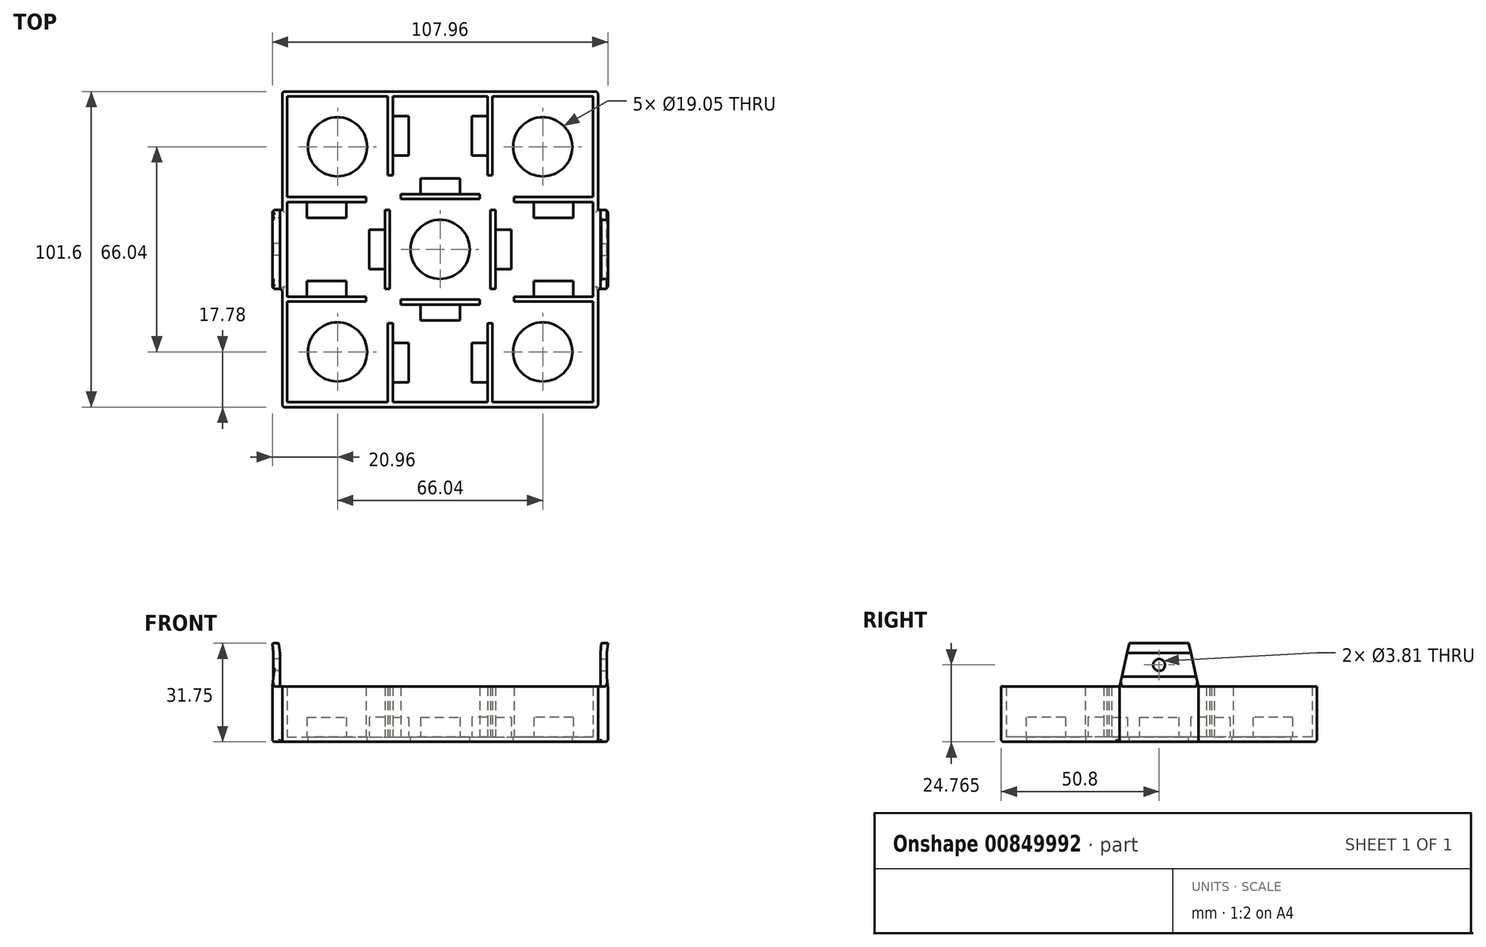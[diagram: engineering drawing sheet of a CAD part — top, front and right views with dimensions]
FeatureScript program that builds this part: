
annotation { "Feature Type Name" : "Feature", "Feature Type Description" : "" }
export const myFeature = defineFeature(function(context is Context, id is Id, definition is map)
    precondition{}
    {
        {
            var Q0;
            Q0=qCreatedBy(makeId("Top.planeOp"),FACE);
            var sketch = newSketch(context, id + "F0", { "sketchPlane" : qUnion([Q0])});
            skLineSegment(sketch, "E0.bottom", {"start": v(-50.8, 50.8) * mm, "end": v(50.8, 50.8) * mm});
            skLineSegment(sketch, "E0.top", {"start": v(-50.8, -50.8) * mm, "end": v(50.8, -50.8) * mm});
            skLineSegment(sketch, "E0.left", {"start": v(-50.8, 50.8) * mm, "end": v(-50.8, -50.8) * mm});
            skLineSegment(sketch, "E0.right", {"start": v(50.8, 50.8) * mm, "end": v(50.8, -50.8) * mm});
            skLineSegment(sketch, "E1", {"start": v(-50.8, 50.8) * mm, "end": v(50.8, -50.8) * mm, "construction": true});
            skSolve(sketch);
        }
        {
            var Q0;
            Q0=qSketchRegion(id+"F0",true);
            extrude(context, id + "F1", {"entities" : qUnion([Q0]), "depth" : 1.59 * mm, "offsetDistance" : 25.4 * mm});
        }
        {
            var Q0;
            Q0=makeQuery(id+"F1.opExtrude","CAP_FACE",FACE,{"disambiguationData":[OSD([sQuery(id+"F0.wireOp",EDGE,"E0.bottom"),sQuery(id+"F0.wireOp",EDGE,"E0.top"),sQuery(id+"F0.wireOp",EDGE,"E0.left"),sQuery(id+"F0.wireOp",EDGE,"E0.right")])],"isStart":false});
            var sketch = newSketch(context, id + "F2", { "sketchPlane" : qUnion([Q0])});
            skLineSegment(sketch, "E2.bottom", {"start": v(-50.8, 50.8) * mm, "end": v(50.8, 50.8) * mm});
            skLineSegment(sketch, "E2.top", {"start": v(-50.8, -50.8) * mm, "end": v(50.8, -50.8) * mm});
            skLineSegment(sketch, "E2.left", {"start": v(-50.8, 50.8) * mm, "end": v(-50.8, -50.8) * mm});
            skLineSegment(sketch, "E2.right", {"start": v(50.8, 50.8) * mm, "end": v(50.8, -50.8) * mm});
            skLineSegment(sketch, "E3.0", {"start": v(49.21, 49.21) * mm, "end": v(49.21, -49.21) * mm});
            skLineSegment(sketch, "E3.1", {"start": v(-49.21, 49.21) * mm, "end": v(49.21, 49.21) * mm});
            skLineSegment(sketch, "E3.2", {"start": v(-49.21, 49.21) * mm, "end": v(-49.21, -49.21) * mm});
            skLineSegment(sketch, "E3.3", {"start": v(-49.21, -49.21) * mm, "end": v(49.21, -49.21) * mm});
            skSolve(sketch);
        }
        {
            var Q0;
            Q0=qSketchRegion(id+"F2",true);
            extrude(context, id + "F3", {"entities" : qUnion([Q0]), "operationType" : NewBodyOperationType.ADD, "depth" : 16.2 * mm, "offsetDistance" : 25.4 * mm});
        }
        {
            var Q0;
            Q0=makeQuery(id+"F1.opExtrude","CAP_FACE",FACE,{"disambiguationData":[OSD([sQuery(id+"F0.wireOp",EDGE,"E0.bottom"),sQuery(id+"F0.wireOp",EDGE,"E0.top"),sQuery(id+"F0.wireOp",EDGE,"E0.left"),sQuery(id+"F0.wireOp",EDGE,"E0.right")])],"isStart":false});
            var sketch = newSketch(context, id + "F4", { "sketchPlane" : qUnion([Q0])});
            skLineSegment(sketch, "E4", {"start": v(-49.21, -16.83) * mm, "end": v(-23.81, -16.83) * mm});
            skLineSegment(sketch, "E5", {"start": v(-49.21, -15.24) * mm, "end": v(-23.81, -15.24) * mm});
            skLineSegment(sketch, "E6", {"start": v(-49.21, -15.24) * mm, "end": v(-49.21, -16.83) * mm});
            skLineSegment(sketch, "E7", {"start": v(49.21, -15.24) * mm, "end": v(49.21, -16.83) * mm});
            skLineSegment(sketch, "E8.bottom", {"start": v(-49.21, 16.83) * mm, "end": v(-23.81, 16.83) * mm});
            skLineSegment(sketch, "E8.top", {"start": v(-49.21, 15.24) * mm, "end": v(-23.81, 15.24) * mm});
            skLineSegment(sketch, "E8.left", {"start": v(-49.21, 16.83) * mm, "end": v(-49.21, 15.24) * mm});
            skLineSegment(sketch, "E8.right", {"start": v(49.21, 16.83) * mm, "end": v(49.21, 15.24) * mm});
            skLineSegment(sketch, "E9.bottom", {"start": v(15.24, 49.21) * mm, "end": v(16.83, 49.21) * mm});
            skLineSegment(sketch, "E9.left", {"start": v(15.24, 49.21) * mm, "end": v(15.24, 23.81) * mm});
            skLineSegment(sketch, "E9.right", {"start": v(16.83, 49.21) * mm, "end": v(16.83, 23.81) * mm});
            skLineSegment(sketch, "E10.bottom", {"start": v(-16.83, 49.21) * mm, "end": v(-15.24, 49.21) * mm});
            skLineSegment(sketch, "E10.left", {"start": v(-16.83, 49.21) * mm, "end": v(-16.83, 23.81) * mm});
            skLineSegment(sketch, "E10.right", {"start": v(-15.24, 49.21) * mm, "end": v(-15.24, 23.81) * mm});
            skLineSegment(sketch, "E11.top", {"start": v(-16.83, -49.21) * mm, "end": v(-15.24, -49.21) * mm});
            skLineSegment(sketch, "E11.left", {"start": v(-16.83, -23.81) * mm, "end": v(-16.83, -49.21) * mm});
            skLineSegment(sketch, "E11.right", {"start": v(-15.24, -23.81) * mm, "end": v(-15.24, -49.21) * mm});
            skLineSegment(sketch, "E12.top", {"start": v(15.24, -49.21) * mm, "end": v(16.83, -49.21) * mm});
            skLineSegment(sketch, "E12.left", {"start": v(15.24, -23.81) * mm, "end": v(15.24, -49.21) * mm});
            skLineSegment(sketch, "E12.right", {"start": v(16.83, -23.81) * mm, "end": v(16.83, -49.21) * mm});
            skLineSegment(sketch, "E13", {"start": v(-23.81, 16.83) * mm, "end": v(-23.81, 15.24) * mm});
            skLineSegment(sketch, "E14", {"start": v(-16.83, 23.81) * mm, "end": v(-15.24, 23.81) * mm});
            skLineSegment(sketch, "E15", {"start": v(15.24, 23.81) * mm, "end": v(16.83, 23.81) * mm});
            skLineSegment(sketch, "E16", {"start": v(23.81, 16.83) * mm, "end": v(23.81, 15.24) * mm});
            skLineSegment(sketch, "E17.trimOffspring", {"start": v(23.81, 16.83) * mm, "end": v(49.21, 16.83) * mm});
            skLineSegment(sketch, "E18.trimOffspring", {"start": v(23.81, 15.24) * mm, "end": v(49.21, 15.24) * mm});
            skLineSegment(sketch, "E19", {"start": v(-16.83, -23.81) * mm, "end": v(-15.24, -23.81) * mm});
            skLineSegment(sketch, "E20", {"start": v(-23.81, -15.24) * mm, "end": v(-23.81, -16.83) * mm});
            skLineSegment(sketch, "E21", {"start": v(49.21, -15.24) * mm, "end": v(23.81, -15.24) * mm});
            skLineSegment(sketch, "E22", {"start": v(23.81, -15.24) * mm, "end": v(23.81, -16.83) * mm});
            skLineSegment(sketch, "E23", {"start": v(23.81, -16.83) * mm, "end": v(49.21, -16.83) * mm});
            skLineSegment(sketch, "E24", {"start": v(15.24, -23.81) * mm, "end": v(16.83, -23.81) * mm});
            skLineSegment(sketch, "E25.bottom", {"start": v(-12.7, 16.2) * mm, "end": v(12.7, 16.2) * mm});
            skLineSegment(sketch, "E25.top", {"start": v(-12.7, -16.2) * mm, "end": v(12.7, -16.2) * mm});
            skLineSegment(sketch, "E25.left", {"start": v(-16.2, 12.7) * mm, "end": v(-16.2, -12.7) * mm});
            skLineSegment(sketch, "E25.right", {"start": v(16.2, 12.7) * mm, "end": v(16.2, -12.7) * mm});
            skLineSegment(sketch, "E26", {"start": v(-12.7, 16.2) * mm, "end": v(-12.7, 17.78) * mm});
            skLineSegment(sketch, "E27", {"start": v(-12.7, 17.78) * mm, "end": v(12.7, 17.78) * mm});
            skLineSegment(sketch, "E28", {"start": v(12.7, 17.78) * mm, "end": v(12.7, 16.2) * mm});
            skLineSegment(sketch, "E29", {"start": v(0, 17.78) * mm, "end": v(0, 16.2) * mm, "construction": true});
            skLineSegment(sketch, "E30", {"start": v(-12.7, -16.2) * mm, "end": v(-12.7, -17.78) * mm});
            skLineSegment(sketch, "E31", {"start": v(-12.7, -17.78) * mm, "end": v(12.7, -17.78) * mm});
            skLineSegment(sketch, "E32", {"start": v(12.7, -17.78) * mm, "end": v(12.7, -16.2) * mm});
            skLineSegment(sketch, "E33", {"start": v(0, -16.2) * mm, "end": v(0, -17.78) * mm, "construction": true});
            skLineSegment(sketch, "E34", {"start": v(16.2, 12.7) * mm, "end": v(17.78, 12.7) * mm});
            skLineSegment(sketch, "E35", {"start": v(17.78, 12.7) * mm, "end": v(17.78, -12.7) * mm});
            skLineSegment(sketch, "E36", {"start": v(17.78, -12.7) * mm, "end": v(16.2, -12.7) * mm});
            skLineSegment(sketch, "E37", {"start": v(16.2, 0) * mm, "end": v(17.78, 0) * mm, "construction": true});
            skLineSegment(sketch, "E38", {"start": v(-16.2, -12.7) * mm, "end": v(-17.78, -12.7) * mm});
            skLineSegment(sketch, "E39", {"start": v(-17.78, -12.7) * mm, "end": v(-17.78, 12.7) * mm});
            skLineSegment(sketch, "E40", {"start": v(-17.78, 12.7) * mm, "end": v(-16.2, 12.7) * mm});
            skLineSegment(sketch, "E41", {"start": v(-16.2, 0) * mm, "end": v(-17.78, 0) * mm, "construction": true});
            skLineSegment(sketch, "E42", {"start": v(0, 16.2) * mm, "end": v(0, 0) * mm, "construction": true});
            skLineSegment(sketch, "E43", {"start": v(0, 0) * mm, "end": v(0, -16.2) * mm, "construction": true});
            skLineSegment(sketch, "E44", {"start": v(-16.2, 0) * mm, "end": v(0, 0) * mm, "construction": true});
            skLineSegment(sketch, "E45", {"start": v(16.2, 0) * mm, "end": v(0, 0) * mm, "construction": true});
            skLineSegment(sketch, "E46", {"start": v(0, 49.21) * mm, "end": v(0, 17.78) * mm, "construction": true});
            skLineSegment(sketch, "E47", {"start": v(0, -17.78) * mm, "end": v(0, -49.21) * mm, "construction": true});
            skLineSegment(sketch, "E48", {"start": v(-49.21, 0) * mm, "end": v(-17.78, 0) * mm, "construction": true});
            skLineSegment(sketch, "E49", {"start": v(17.78, 0) * mm, "end": v(49.21, 0) * mm, "construction": true});
            skSolve(sketch);
        }
        {
            var Q0;
            Q0=qSketchRegion(id+"F4",true);
            var Q1;
            Q1=makeQuery(id+"F3.opExtrude","CAP_FACE",FACE,{"disambiguationData":[OSD([sQuery(id+"F2.wireOp",EDGE,"E2.bottom"),sQuery(id+"F2.wireOp",EDGE,"E2.top"),sQuery(id+"F2.wireOp",EDGE,"E2.left"),sQuery(id+"F2.wireOp",EDGE,"E2.right"),sQuery(id+"F2.wireOp",EDGE,"E3.0"),sQuery(id+"F2.wireOp",EDGE,"E3.1"),sQuery(id+"F2.wireOp",EDGE,"E3.2"),sQuery(id+"F2.wireOp",EDGE,"E3.3")])],"isStart":false});
            extrude(context, id + "F5", {"entities" : qUnion([Q0]), "operationType" : NewBodyOperationType.ADD, "endBound" : BoundingType.UP_TO_SURFACE, "depth" : 25.4 * mm, "endBoundEntityFace" : qUnion([Q1]), "offsetDistance" : 25.4 * mm});
        }
        {
            var Q0;
            Q0=makeQuery(id+"F1.opExtrude","CAP_FACE",FACE,{"disambiguationData":[OSD([sQuery(id+"F0.wireOp",EDGE,"E0.bottom"),sQuery(id+"F0.wireOp",EDGE,"E0.top"),sQuery(id+"F0.wireOp",EDGE,"E0.left"),sQuery(id+"F0.wireOp",EDGE,"E0.right")])],"isStart":false});
            var sketch = newSketch(context, id + "F6", { "sketchPlane" : qUnion([Q0])});
            skLineSegment(sketch, "E50.bottom", {"start": v(-42.86, 15.24) * mm, "end": v(-30.16, 15.24) * mm});
            skLineSegment(sketch, "E50.top", {"start": v(-42.86, 10.16) * mm, "end": v(-30.16, 10.16) * mm});
            skLineSegment(sketch, "E50.left", {"start": v(-42.86, 15.24) * mm, "end": v(-42.86, 10.16) * mm});
            skLineSegment(sketch, "E50.right", {"start": v(-30.16, 15.24) * mm, "end": v(-30.16, 10.16) * mm});
            skLineSegment(sketch, "E51.bottom", {"start": v(-42.86, -15.24) * mm, "end": v(-30.16, -15.24) * mm});
            skLineSegment(sketch, "E51.top", {"start": v(-42.86, -10.16) * mm, "end": v(-30.16, -10.16) * mm});
            skLineSegment(sketch, "E51.left", {"start": v(-42.86, -15.24) * mm, "end": v(-42.86, -10.16) * mm});
            skLineSegment(sketch, "E51.right", {"start": v(-30.16, -15.24) * mm, "end": v(-30.16, -10.16) * mm});
            skLineSegment(sketch, "E52.bottom", {"start": v(-15.24, 42.86) * mm, "end": v(-10.16, 42.86) * mm});
            skLineSegment(sketch, "E52.top", {"start": v(-15.24, 30.16) * mm, "end": v(-10.16, 30.16) * mm});
            skLineSegment(sketch, "E52.left", {"start": v(-15.24, 42.86) * mm, "end": v(-15.24, 30.16) * mm});
            skLineSegment(sketch, "E52.right", {"start": v(-10.16, 42.86) * mm, "end": v(-10.16, 30.16) * mm});
            skLineSegment(sketch, "E53.bottom", {"start": v(15.24, 42.86) * mm, "end": v(10.16, 42.86) * mm});
            skLineSegment(sketch, "E53.top", {"start": v(15.24, 30.16) * mm, "end": v(10.16, 30.16) * mm});
            skLineSegment(sketch, "E53.left", {"start": v(15.24, 42.86) * mm, "end": v(15.24, 30.16) * mm});
            skLineSegment(sketch, "E53.right", {"start": v(10.16, 42.86) * mm, "end": v(10.16, 30.16) * mm});
            skLineSegment(sketch, "E54.bottom", {"start": v(30.16, 15.24) * mm, "end": v(42.86, 15.24) * mm});
            skLineSegment(sketch, "E54.top", {"start": v(30.16, 10.16) * mm, "end": v(42.86, 10.16) * mm});
            skLineSegment(sketch, "E54.left", {"start": v(30.16, 15.24) * mm, "end": v(30.16, 10.16) * mm});
            skLineSegment(sketch, "E54.right", {"start": v(42.86, 15.24) * mm, "end": v(42.86, 10.16) * mm});
            skLineSegment(sketch, "E55.bottom", {"start": v(30.16, -15.24) * mm, "end": v(42.86, -15.24) * mm});
            skLineSegment(sketch, "E55.top", {"start": v(30.16, -10.16) * mm, "end": v(42.86, -10.16) * mm});
            skLineSegment(sketch, "E55.left", {"start": v(30.16, -15.24) * mm, "end": v(30.16, -10.16) * mm});
            skLineSegment(sketch, "E55.right", {"start": v(42.86, -15.24) * mm, "end": v(42.86, -10.16) * mm});
            skLineSegment(sketch, "E56.bottom", {"start": v(15.24, -30.16) * mm, "end": v(10.16, -30.16) * mm});
            skLineSegment(sketch, "E56.top", {"start": v(15.24, -42.86) * mm, "end": v(10.16, -42.86) * mm});
            skLineSegment(sketch, "E56.left", {"start": v(15.24, -30.16) * mm, "end": v(15.24, -42.86) * mm});
            skLineSegment(sketch, "E56.right", {"start": v(10.16, -30.16) * mm, "end": v(10.16, -42.86) * mm});
            skLineSegment(sketch, "E57.bottom", {"start": v(-15.24, -30.16) * mm, "end": v(-10.16, -30.16) * mm});
            skLineSegment(sketch, "E57.top", {"start": v(-15.24, -42.86) * mm, "end": v(-10.16, -42.86) * mm});
            skLineSegment(sketch, "E57.left", {"start": v(-15.24, -30.16) * mm, "end": v(-15.24, -42.86) * mm});
            skLineSegment(sketch, "E57.right", {"start": v(-10.16, -30.16) * mm, "end": v(-10.16, -42.86) * mm});
            skLineSegment(sketch, "E58.bottom", {"start": v(-6.35, -17.78) * mm, "end": v(6.35, -17.78) * mm});
            skLineSegment(sketch, "E58.top", {"start": v(-6.35, -22.86) * mm, "end": v(6.35, -22.86) * mm});
            skLineSegment(sketch, "E58.left", {"start": v(-6.35, -17.78) * mm, "end": v(-6.35, -22.86) * mm});
            skLineSegment(sketch, "E58.right", {"start": v(6.35, -17.78) * mm, "end": v(6.35, -22.86) * mm});
            skLineSegment(sketch, "E59.bottom", {"start": v(17.78, 6.35) * mm, "end": v(22.86, 6.35) * mm});
            skLineSegment(sketch, "E59.top", {"start": v(17.78, -6.35) * mm, "end": v(22.86, -6.35) * mm});
            skLineSegment(sketch, "E59.left", {"start": v(17.78, 6.35) * mm, "end": v(17.78, -6.35) * mm});
            skLineSegment(sketch, "E59.right", {"start": v(22.86, 6.35) * mm, "end": v(22.86, -6.35) * mm});
            skLineSegment(sketch, "E60.bottom", {"start": v(-17.78, 6.35) * mm, "end": v(-22.86, 6.35) * mm});
            skLineSegment(sketch, "E60.left", {"start": v(-17.78, 6.35) * mm, "end": v(-17.78, -6.35) * mm});
            skLineSegment(sketch, "E61.bottom", {"start": v(-6.35, 17.78) * mm, "end": v(6.35, 17.78) * mm});
            skLineSegment(sketch, "E61.top", {"start": v(-6.35, 22.86) * mm, "end": v(6.35, 22.86) * mm});
            skLineSegment(sketch, "E61.left", {"start": v(-6.35, 17.78) * mm, "end": v(-6.35, 22.86) * mm});
            skLineSegment(sketch, "E61.right", {"start": v(6.35, 17.78) * mm, "end": v(6.35, 22.86) * mm});
            skLineSegment(sketch, "E62", {"start": v(-22.86, 6.35) * mm, "end": v(-22.86, -6.35) * mm});
            skLineSegment(sketch, "E63", {"start": v(-22.86, -6.35) * mm, "end": v(-17.78, -6.35) * mm});
            skSolve(sketch);
        }
        {
            var Q0;
            Q0=qSketchRegion(id+"F6",true);
            extrude(context, id + "F7", {"entities" : qUnion([Q0]), "operationType" : NewBodyOperationType.ADD, "depth" : 6.35 * mm, "offsetDistance" : 25.4 * mm});
        }
        {
            var Q0;
            Q0=makeQuery(id+"F1.opExtrude","CAP_FACE",FACE,{"disambiguationData":[OSD([sQuery(id+"F0.wireOp",EDGE,"E0.bottom"),sQuery(id+"F0.wireOp",EDGE,"E0.top"),sQuery(id+"F0.wireOp",EDGE,"E0.left"),sQuery(id+"F0.wireOp",EDGE,"E0.right")])],"isStart":false});
            var sketch = newSketch(context, id + "F8", { "sketchPlane" : qUnion([Q0])});
            skCircle(sketch, "E64", {"center": v(0, 0) * mm, "radius": 9.53 * mm});
            skCircle(sketch, "E65", {"center": v(-33.02, 33.02) * mm, "radius": 9.53 * mm});
            skCircle(sketch, "E66", {"center": v(33.02, 33.02) * mm, "radius": 9.53 * mm});
            skCircle(sketch, "E67", {"center": v(33.02, -33.02) * mm, "radius": 9.53 * mm});
            skCircle(sketch, "E68", {"center": v(-33.02, -33.02) * mm, "radius": 9.53 * mm});
            skPoint(sketch, "E68.centerSnap0", {"position": v(-16.83, -36.51) * mm});
            skSolve(sketch);
        }
        {
            var Q0;
            Q0 = qSketchRegion(id + "F8", true);
            extrude(context, id + "F9", {"entities" : qUnion([Q0]), "operationType" : NewBodyOperationType.REMOVE, "oppositeDirection" : true, "depth" : 25.4 * mm, "offsetDistance" : 25.4 * mm});
        }
        {
            var Q0;
            Q0=qCreatedBy(makeId("Front.planeOp"),FACE);
            var sketch = newSketch(context, id + "F10", { "sketchPlane" : qUnion([Q0])});
            skLineSegment(sketch, "E69.bottom", {"start": v(53.98, 0) * mm, "end": v(50.8, 0) * mm});
            skLineSegment(sketch, "E69.top", {"start": v(53.98, 31.75) * mm, "end": v(51.91, 31.75) * mm});
            skLineSegment(sketch, "E69.left", {"start": v(53.98, 0) * mm, "end": v(53.98, 17.78) * mm});
            skLineSegment(sketch, "E69.right", {"start": v(50.8, 0) * mm, "end": v(50.8, 17.78) * mm});
            skLineSegment(sketch, "E70", {"start": v(51.91, 31.75) * mm, "end": v(51.56, 28.57) * mm});
            skLineSegment(sketch, "E71", {"start": v(51.56, 28.58) * mm, "end": v(51.56, 17.78) * mm});
            skLineSegment(sketch, "E72", {"start": v(51.56, 17.78) * mm, "end": v(50.8, 17.78) * mm});
            skLineSegment(sketch, "E73", {"start": v(53.98, 31.75) * mm, "end": v(53.63, 28.57) * mm});
            skLineSegment(sketch, "E74", {"start": v(53.63, 28.57) * mm, "end": v(53.63, 20.96) * mm});
            skLineSegment(sketch, "E75", {"start": v(53.63, 20.96) * mm, "end": v(53.98, 17.78) * mm});
            skSolve(sketch);
        }
        {
            var Q0;
            Q0 = qSketchRegion(id + "F10", true);
            extrude(context, id + "F11", {"entities" : qUnion([Q0]), "operationType" : NewBodyOperationType.ADD, "endBound" : BoundingType.SYMMETRIC, "depth" : 25.4 * mm, "offsetDistance" : 25.4 * mm});
        }
        {
            var Q0;
            Q0=makeQuery(id+"F11.opExtrude","SWEPT_FACE",FACE,{"disambiguationData":[OSD([sQuery(id+"F10.wireOp",EDGE,"E69.left")])]});
            var sketch = newSketch(context, id + "F12", { "sketchPlane" : qUnion([Q0])});
            skLineSegment(sketch, "E76", {"start": v(-12.7, 17.78) * mm, "end": v(-9.53, 31.75) * mm});
            skLineSegment(sketch, "E77", {"start": v(-9.53, 31.75) * mm, "end": v(-12.7, 31.75) * mm});
            skLineSegment(sketch, "E78", {"start": v(-12.7, 31.75) * mm, "end": v(-12.7, 17.78) * mm});
            skLineSegment(sketch, "E79", {"start": v(12.7, 17.78) * mm, "end": v(9.52, 31.75) * mm});
            skLineSegment(sketch, "E80", {"start": v(9.53, 31.75) * mm, "end": v(12.7, 31.75) * mm});
            skLineSegment(sketch, "E81", {"start": v(12.7, 31.75) * mm, "end": v(12.7, 17.78) * mm});
            skSolve(sketch);
        }
        {
            var Q0;
            Q0 = qSketchRegion(id + "F12", true);
            extrude(context, id + "F13", {"entities" : qUnion([Q0]), "operationType" : NewBodyOperationType.REMOVE, "oppositeDirection" : true, "depth" : 3.17 * mm, "offsetDistance" : 25.4 * mm});
        }
        {
            var Q0;
            Q0=makeQuery(id+"F11.opExtrude","SWEPT_FACE",FACE,{"disambiguationData":[OSD([sQuery(id+"F10.wireOp",EDGE,"E74")])]});
            var sketch = newSketch(context, id + "F14", { "sketchPlane" : qUnion([Q0])});
            skCircle(sketch, "E82", {"center": v(0, 24.76) * mm, "radius": 1.9 * mm});
            skLineSegment(sketch, "E83", {"start": v(0, 28.57) * mm, "end": v(0, 24.76) * mm, "construction": true});
            skLineSegment(sketch, "E84", {"start": v(0, 20.95) * mm, "end": v(0, 24.76) * mm, "construction": true});
            skSolve(sketch);
        }
        {
            var Q0;
            Q0 = qSketchRegion(id + "F14", true);
            extrude(context, id + "F15", {"entities" : qUnion([Q0]), "operationType" : NewBodyOperationType.REMOVE, "oppositeDirection" : true, "depth" : 25.4 * mm, "offsetDistance" : 25.4 * mm});
        }
        {
            var Q0;
            Q0=makeQuery(id+"F1.opExtrude","SWEPT_BODY",BODY,{"disambiguationData":[OSD([sQuery(id+"F0.wireOp",EDGE,"E0.bottom"),sQuery(id+"F0.wireOp",EDGE,"E0.top"),sQuery(id+"F0.wireOp",EDGE,"E0.left"),sQuery(id+"F0.wireOp",EDGE,"E0.right")])]});
            var Q1;
            Q1=qCreatedBy(makeId("Right.planeOp"),FACE);
            mirror(context, id + "F16", {"operationType" : NewBodyOperationType.ADD, "entities" : qUnion([Q0]), "mirrorPlane" : qUnion([Q1])});
        }
        {
            var Q0;
            Q0=makeQuery(id+"F3.boolean.opBoolean","MERGE",EDGE,{"derivedFrom":[makeQuery(id+"F1.opExtrude","SWEPT_EDGE",EDGE,{"disambiguationData":[OSD([sQuery(id+"F0.wireOp",EDGE,"E0.bottom"),sQuery(id+"F0.wireOp",EDGE,"E0.left")])]}),makeQuery(id+"F3.opExtrude","SWEPT_EDGE",EDGE,{"disambiguationData":[OSD([sQuery(id+"F2.wireOp",EDGE,"E2.bottom"),sQuery(id+"F2.wireOp",EDGE,"E2.left")])]})]});
            var Q1;
            Q1=makeQuery(id+"F1.opExtrude","CAP_EDGE",EDGE,{"disambiguationData":[OSD([sQuery(id+"F0.wireOp",EDGE,"E0.bottom")])],"isStart":true});
            var Q2;
            {var subQ0=sQuery(id+"F0.wireOp",EDGE,"E0.left");var subQ1=sQuery(id+"F0.wireOp",EDGE,"E0.bottom");Q2=makeQuery(id+"F16.boolean.opBoolean","SPLIT",EDGE,{"disambiguationData":[TD([makeQuery(id+"F1.opExtrude","SWEPT_FACE",FACE,{"disambiguationData":[OSD([subQ1])]})])],"derivedFrom":makeQuery(id+"F1.opExtrude","CAP_EDGE",EDGE,{"disambiguationData":[OSD([subQ0])],"isStart":true})});}
            var Q3;
            Q3=makeQuery(id+"F16.opPattern","COPY",EDGE,{"derivedFrom":makeQuery(id+"F11.opExtrude","SWEPT_EDGE",EDGE,{"disambiguationData":[OSD([sQuery(id+"F10.wireOp",EDGE,"E69.bottom"),sQuery(id+"F10.wireOp",EDGE,"E69.left")])]}),"instanceName":"1"});
            var Q4;
            Q4=makeQuery(id+"F16.opPattern","COPY",EDGE,{"derivedFrom":makeQuery(id+"F11.opExtrude","CAP_EDGE",EDGE,{"disambiguationData":[OSD([sQuery(id+"F10.wireOp",EDGE,"E69.bottom")])],"isStart":true}),"instanceName":"1"});
            var Q5;
            Q5=makeQuery(id+"F16.opPattern","COPY",EDGE,{"derivedFrom":makeQuery(id+"F11.opExtrude","CAP_EDGE",EDGE,{"disambiguationData":[OSD([sQuery(id+"F10.wireOp",EDGE,"E69.bottom")])],"isStart":false}),"instanceName":"1"});
            var Q6;
            {var subQ0=sQuery(id+"F0.wireOp",EDGE,"E0.left");var subQ1=sQuery(id+"F0.wireOp",EDGE,"E0.top");Q6=makeQuery(id+"F16.boolean.opBoolean","SPLIT",EDGE,{"disambiguationData":[TD([makeQuery(id+"F1.opExtrude","SWEPT_FACE",FACE,{"disambiguationData":[OSD([subQ1])]})])],"derivedFrom":makeQuery(id+"F1.opExtrude","CAP_EDGE",EDGE,{"disambiguationData":[OSD([subQ0])],"isStart":true})});}
            var Q7;
            Q7=makeQuery(id+"F3.boolean.opBoolean","MERGE",EDGE,{"derivedFrom":[makeQuery(id+"F1.opExtrude","SWEPT_EDGE",EDGE,{"disambiguationData":[OSD([sQuery(id+"F0.wireOp",EDGE,"E0.top"),sQuery(id+"F0.wireOp",EDGE,"E0.left")])]}),makeQuery(id+"F3.opExtrude","SWEPT_EDGE",EDGE,{"disambiguationData":[OSD([sQuery(id+"F2.wireOp",EDGE,"E2.top"),sQuery(id+"F2.wireOp",EDGE,"E2.left")])]})]});
            var Q8;
            Q8=makeQuery(id+"F1.opExtrude","CAP_EDGE",EDGE,{"disambiguationData":[OSD([sQuery(id+"F0.wireOp",EDGE,"E0.top")])],"isStart":true});
            var Q9;
            Q9=makeQuery(id+"F3.boolean.opBoolean","MERGE",EDGE,{"derivedFrom":[makeQuery(id+"F1.opExtrude","SWEPT_EDGE",EDGE,{"disambiguationData":[OSD([sQuery(id+"F0.wireOp",EDGE,"E0.top"),sQuery(id+"F0.wireOp",EDGE,"E0.right")])]}),makeQuery(id+"F3.opExtrude","SWEPT_EDGE",EDGE,{"disambiguationData":[OSD([sQuery(id+"F2.wireOp",EDGE,"E2.top"),sQuery(id+"F2.wireOp",EDGE,"E2.right")])]})]});
            var Q10;
            {var subQ0=sQuery(id+"F0.wireOp",EDGE,"E0.right");var subQ1=sQuery(id+"F0.wireOp",EDGE,"E0.top");Q10=makeQuery(id+"F11.boolean.opBoolean","SPLIT",EDGE,{"disambiguationData":[TD([makeQuery(id+"F1.opExtrude","SWEPT_FACE",FACE,{"disambiguationData":[OSD([subQ1])]})])],"derivedFrom":makeQuery(id+"F1.opExtrude","CAP_EDGE",EDGE,{"disambiguationData":[OSD([subQ0])],"isStart":true})});}
            var Q11;
            Q11=makeQuery(id+"F11.opExtrude","CAP_EDGE",EDGE,{"disambiguationData":[OSD([sQuery(id+"F10.wireOp",EDGE,"E69.bottom")])],"isStart":false});
            var Q12;
            Q12=makeQuery(id+"F11.opExtrude","SWEPT_EDGE",EDGE,{"disambiguationData":[OSD([sQuery(id+"F10.wireOp",EDGE,"E69.bottom"),sQuery(id+"F10.wireOp",EDGE,"E69.left")])]});
            var Q13;
            Q13=makeQuery(id+"F11.opExtrude","CAP_EDGE",EDGE,{"disambiguationData":[OSD([sQuery(id+"F10.wireOp",EDGE,"E69.bottom")])],"isStart":true});
            var Q14;
            {var subQ0=sQuery(id+"F0.wireOp",EDGE,"E0.right");var subQ1=sQuery(id+"F0.wireOp",EDGE,"E0.bottom");Q14=makeQuery(id+"F11.boolean.opBoolean","SPLIT",EDGE,{"disambiguationData":[TD([makeQuery(id+"F1.opExtrude","SWEPT_FACE",FACE,{"disambiguationData":[OSD([subQ1])]})])],"derivedFrom":makeQuery(id+"F1.opExtrude","CAP_EDGE",EDGE,{"disambiguationData":[OSD([subQ0])],"isStart":true})});}
            var Q15;
            Q15=makeQuery(id+"F3.boolean.opBoolean","MERGE",EDGE,{"derivedFrom":[makeQuery(id+"F1.opExtrude","SWEPT_EDGE",EDGE,{"disambiguationData":[OSD([sQuery(id+"F0.wireOp",EDGE,"E0.bottom"),sQuery(id+"F0.wireOp",EDGE,"E0.right")])]}),makeQuery(id+"F3.opExtrude","SWEPT_EDGE",EDGE,{"disambiguationData":[OSD([sQuery(id+"F2.wireOp",EDGE,"E2.bottom"),sQuery(id+"F2.wireOp",EDGE,"E2.right")])]})]});
            fillet(context, id + "F17", {"entities" : qUnion([Q0, Q1, Q2, Q3, Q4, Q5, Q6, Q7, Q8, Q9, Q10, Q11, Q12, Q13, Q14, Q15]), "radius" : 0.83 * mm, "tangentPropagation" : true, "allowEdgeOverflow" : false});
        }
        {
            var Q0;
            Q0=makeQuery(id+"F16.opPattern","COPY",EDGE,{"derivedFrom":makeQuery(id+"F11.opExtrude","CAP_EDGE",EDGE,{"disambiguationData":[OSD([sQuery(id+"F10.wireOp",EDGE,"E69.left")])],"isStart":true}),"instanceName":"1"});
            var Q1;
            Q1=makeQuery(id+"F16.opPattern","COPY",EDGE,{"derivedFrom":makeQuery(id+"F11.opExtrude","CAP_EDGE",EDGE,{"disambiguationData":[OSD([sQuery(id+"F10.wireOp",EDGE,"E69.right")])],"isStart":true}),"instanceName":"1"});
            var Q2;
            Q2=makeQuery(id+"F16.opPattern","COPY",EDGE,{"derivedFrom":makeQuery(id+"F11.opExtrude","CAP_EDGE",EDGE,{"disambiguationData":[OSD([sQuery(id+"F10.wireOp",EDGE,"E69.left")])],"isStart":false}),"instanceName":"1"});
            var Q3;
            Q3=makeQuery(id+"F16.opPattern","COPY",EDGE,{"derivedFrom":makeQuery(id+"F11.opExtrude","CAP_EDGE",EDGE,{"disambiguationData":[OSD([sQuery(id+"F10.wireOp",EDGE,"E69.right")])],"isStart":false}),"instanceName":"1"});
            var Q4;
            Q4=makeQuery(id+"F11.opExtrude","CAP_EDGE",EDGE,{"disambiguationData":[OSD([sQuery(id+"F10.wireOp",EDGE,"E69.left")])],"isStart":false});
            var Q5;
            Q5=makeQuery(id+"F11.opExtrude","CAP_EDGE",EDGE,{"disambiguationData":[OSD([sQuery(id+"F10.wireOp",EDGE,"E69.right")])],"isStart":false});
            var Q6;
            Q6=makeQuery(id+"F11.opExtrude","CAP_EDGE",EDGE,{"disambiguationData":[OSD([sQuery(id+"F10.wireOp",EDGE,"E69.right")])],"isStart":true});
            var Q7;
            Q7=makeQuery(id+"F11.opExtrude","CAP_EDGE",EDGE,{"disambiguationData":[OSD([sQuery(id+"F10.wireOp",EDGE,"E69.left")])],"isStart":true});
            fillet(context, id + "F18", {"entities" : qUnion([Q0, Q1, Q2, Q3, Q4, Q5, Q6, Q7]), "radius" : 0.95 * mm, "tangentPropagation" : true, "allowEdgeOverflow" : false});
        }
        {
            var Q0;
            Q0=makeQuery(id+"F16.opPattern","COPY",EDGE,{"derivedFrom":makeQuery(id+"F13.boolean.opBoolean","INTERSECT",EDGE,{"derivedFrom":[makeQuery(id+"F11.opExtrude","SWEPT_FACE",FACE,{"disambiguationData":[OSD([sQuery(id+"F10.wireOp",EDGE,"E71")])]}),makeQuery(id+"F13.opExtrude","SWEPT_FACE",FACE,{"disambiguationData":[OSD([sQuery(id+"F12.wireOp",EDGE,"E79")])]})]}),"instanceName":"1"});
            var Q1;
            Q1=makeQuery(id+"F16.opPattern","COPY",EDGE,{"derivedFrom":makeQuery(id+"F13.boolean.opBoolean","INTERSECT",EDGE,{"derivedFrom":[makeQuery(id+"F11.opExtrude","SWEPT_FACE",FACE,{"disambiguationData":[OSD([sQuery(id+"F10.wireOp",EDGE,"E70")])]}),makeQuery(id+"F13.opExtrude","SWEPT_FACE",FACE,{"disambiguationData":[OSD([sQuery(id+"F12.wireOp",EDGE,"E79")])]})]}),"instanceName":"1"});
            var Q2;
            Q2=makeQuery(id+"F16.opPattern","COPY",EDGE,{"derivedFrom":makeQuery(id+"F13.boolean.opBoolean","COPY",EDGE,{"derivedFrom":makeQuery(id+"F13.opExtrude","SWEPT_EDGE",EDGE,{"disambiguationData":[OSD([sQuery(id+"F12.wireOp",EDGE,"E79"),sQuery(id+"F12.wireOp",EDGE,"E80")])]})}),"instanceName":"1"});
            var Q3;
            Q3=makeQuery(id+"F16.opPattern","COPY",EDGE,{"derivedFrom":makeQuery(id+"F11.opExtrude","SWEPT_EDGE",EDGE,{"disambiguationData":[OSD([sQuery(id+"F10.wireOp",EDGE,"E69.top"),sQuery(id+"F10.wireOp",EDGE,"E70")])]}),"instanceName":"1"});
            var Q4;
            Q4=makeQuery(id+"F16.opPattern","COPY",EDGE,{"derivedFrom":makeQuery(id+"F13.boolean.opBoolean","INTERSECT",EDGE,{"derivedFrom":[makeQuery(id+"F11.opExtrude","SWEPT_FACE",FACE,{"disambiguationData":[OSD([sQuery(id+"F10.wireOp",EDGE,"E70")])]}),makeQuery(id+"F13.opExtrude","SWEPT_FACE",FACE,{"disambiguationData":[OSD([sQuery(id+"F12.wireOp",EDGE,"E76")])]})]}),"instanceName":"1"});
            var Q5;
            Q5=makeQuery(id+"F16.opPattern","COPY",EDGE,{"derivedFrom":makeQuery(id+"F13.boolean.opBoolean","INTERSECT",EDGE,{"derivedFrom":[makeQuery(id+"F11.opExtrude","SWEPT_FACE",FACE,{"disambiguationData":[OSD([sQuery(id+"F10.wireOp",EDGE,"E71")])]}),makeQuery(id+"F13.opExtrude","SWEPT_FACE",FACE,{"disambiguationData":[OSD([sQuery(id+"F12.wireOp",EDGE,"E76")])]})]}),"instanceName":"1"});
            var Q6;
            Q6=makeQuery(id+"F16.opPattern","COPY",EDGE,{"derivedFrom":makeQuery(id+"F13.boolean.opBoolean","COPY",EDGE,{"derivedFrom":makeQuery(id+"F13.opExtrude","SWEPT_EDGE",EDGE,{"disambiguationData":[OSD([sQuery(id+"F12.wireOp",EDGE,"E76"),sQuery(id+"F12.wireOp",EDGE,"E77")])]})}),"instanceName":"1"});
            var Q7;
            Q7=makeQuery(id+"F16.opPattern","COPY",EDGE,{"derivedFrom":makeQuery(id+"F11.opExtrude","SWEPT_EDGE",EDGE,{"disambiguationData":[OSD([sQuery(id+"F10.wireOp",EDGE,"E69.top"),sQuery(id+"F10.wireOp",EDGE,"E73")])]}),"instanceName":"1"});
            fillet(context, id + "F19", {"entities" : qUnion([Q0, Q1, Q2, Q3, Q4, Q5, Q6, Q7]), "radius" : 0.32 * mm, "tangentPropagation" : true, "allowEdgeOverflow" : false});
        }
        {
            var Q0;
            Q0=makeQuery(id+"F16.opPattern","COPY",EDGE,{"derivedFrom":makeQuery(id+"F13.boolean.opBoolean","INTERSECT",EDGE,{"derivedFrom":[makeQuery(id+"F11.opExtrude","SWEPT_FACE",FACE,{"disambiguationData":[OSD([sQuery(id+"F10.wireOp",EDGE,"E74")])]}),makeQuery(id+"F13.opExtrude","SWEPT_FACE",FACE,{"disambiguationData":[OSD([sQuery(id+"F12.wireOp",EDGE,"E79")])]})]}),"instanceName":"1"});
            var Q1;
            Q1=makeQuery(id+"F16.opPattern","COPY",EDGE,{"derivedFrom":makeQuery(id+"F13.boolean.opBoolean","INTERSECT",EDGE,{"derivedFrom":[makeQuery(id+"F11.opExtrude","SWEPT_FACE",FACE,{"disambiguationData":[OSD([sQuery(id+"F10.wireOp",EDGE,"E74")])]}),makeQuery(id+"F13.opExtrude","SWEPT_FACE",FACE,{"disambiguationData":[OSD([sQuery(id+"F12.wireOp",EDGE,"E76")])]})]}),"instanceName":"1"});
            var Q2;
            Q2=makeQuery(id+"F16.opPattern","COPY",EDGE,{"derivedFrom":makeQuery(id+"F13.boolean.opBoolean","INTERSECT",EDGE,{"derivedFrom":[makeQuery(id+"F11.opExtrude","SWEPT_FACE",FACE,{"disambiguationData":[OSD([sQuery(id+"F10.wireOp",EDGE,"E73")])]}),makeQuery(id+"F13.opExtrude","SWEPT_FACE",FACE,{"disambiguationData":[OSD([sQuery(id+"F12.wireOp",EDGE,"E76")])]})]}),"instanceName":"1"});
            var Q3;
            Q3=makeQuery(id+"F16.opPattern","COPY",EDGE,{"derivedFrom":makeQuery(id+"F13.boolean.opBoolean","INTERSECT",EDGE,{"derivedFrom":[makeQuery(id+"F11.opExtrude","SWEPT_FACE",FACE,{"disambiguationData":[OSD([sQuery(id+"F10.wireOp",EDGE,"E73")])]}),makeQuery(id+"F13.opExtrude","SWEPT_FACE",FACE,{"disambiguationData":[OSD([sQuery(id+"F12.wireOp",EDGE,"E79")])]})]}),"instanceName":"1"});
            fillet(context, id + "F20", {"entities" : qUnion([Q0, Q1, Q2, Q3]), "radius" : 0.32 * mm, "tangentPropagation" : true, "allowEdgeOverflow" : false});
        }
    });
